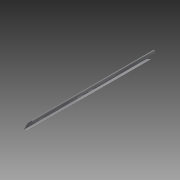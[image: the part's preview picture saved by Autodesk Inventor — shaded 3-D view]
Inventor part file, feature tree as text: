
AUTODESK INVENTOR PART (.ipt)
format: ipt  version: 2015 SP1 (Build 190203100, 203)  size: 275,456 bytes
history: native  units: in
note: dims shown in document units (in); Inventor stores cm internally (conversion verified against a paired STEP export)
features: sketch x8, projected_geometry x5, extrude x4, hole x4
ambient origin geometry x8: Origin, YZ Plane, XZ Plane, XY Plane, X Axis, Y Axis, Z Axis, Center Point
bodies: Solid1 (feature_tree)
feature tree (21):
  extrude  "Extrusion1"  Depth=2.125in
  hole  "Hole1"  [1 undecoded]
  extrude  "Extrusion2"  TaperAngle=90.0deg  [1 undecoded]
  hole  "Hole2"  [1 undecoded]
  extrude  "Extrusion3"  Depth=0.25in
  hole  "Hole5"  [1 undecoded]
  hole  "Hole6"  [1 undecoded]
  extrude  "Extrusion4"  TaperAngle=90.0deg  [1 undecoded]
  sketch  "Sketch1"  dims[d0=0.5in d1=2.125in]
  sketch  "Sketch2"  dims[d2=0.5in d3=180.0deg]
  projected_geometry  "Projected Loop1"
  sketch  "Sketch3"  dims[d4=2.125in d5=90.0deg]
  projected_geometry  "Projected Loop2"
  sketch  "Sketch4"  dims[d6=0.5in d7=0.5in]
  projected_geometry  "Projected Loop3"
  sketch  "Sketch6"  dims[d8=0.25in d9=0.25in]
  projected_geometry  "Projected Loop5"
  sketch  "Sketch8"  dims[d10=0.25in d11=150.0deg]
  projected_geometry  "Projected Loop7"
  sketch  "Sketch9"  dims[d12=0.25in d13=30.0deg]
  sketch  "Sketch10"  dims[d14=0.0625in d15=90.0deg d16=1.0625in d17=0.25in d18=60.0deg d19=120.0deg d20=90.0deg d21=0.0625in d22=0.25in d23=0.25in d24=0.0625in d25=0.3125in d26=0.0in d27=66.5in d28=0.0in d29=0.75in d30=1.5in d33=0.375in d34=0.75in d35=0.375in d36=0.25in d37=0.5635in d38=1.0in d39=0.8108in d45=0.5in d46=0.625in d47=1.25in d48=0.5in d49=0.625in d50=0.375in d51=0.75in d52=0.5in d53=0.5in d54=1.125in d55=1.125in d56=0.125in d57=0.125in d58=0.125in d59=0.125in d60=0.125in d61=0.125in d62=0.125in d63=0.125in d64=0.125in d65=0.125in d66=0.125in d67=0.125in d68=1.0in d69=0.0in d70=2.5in d71=3.0in d72=3.5in d73=4.0in d74=0.5in d77=0.5in d78=0.25in d79=0.75in d80=0.375in d81=0.25in d82=0.5635in d83=1.0in d84=0.8108in d98=2.0in d99=1.0in d100=2.0in d101=1.0in d102=31.0in d103=35.5in d104=0.25in d105=0.25in d106=1.0in d107=0.0in d120=1.0in d121=1.0in d122=0.75in d123=0.75in d124=7.5in d125=30.5in d126=0.25in d127=0.75in d128=0.375in d129=0.25in d130=0.5635in d131=1.0in d132=0.8108in d135=0.5in d136=0.5in d137=0.5in d138=1.0in d139=0.25in d140=0.75in d141=0.375in d142=0.25in d143=0.5635in d144=1.0in d145=0.8108in d146=0.75in d147=0.0in]
note: 6 required parameter values undecoded (feature->parameter linkage not recoverable at this tier; creation-order binding heuristic only, values carry confidence <= 0.55)
